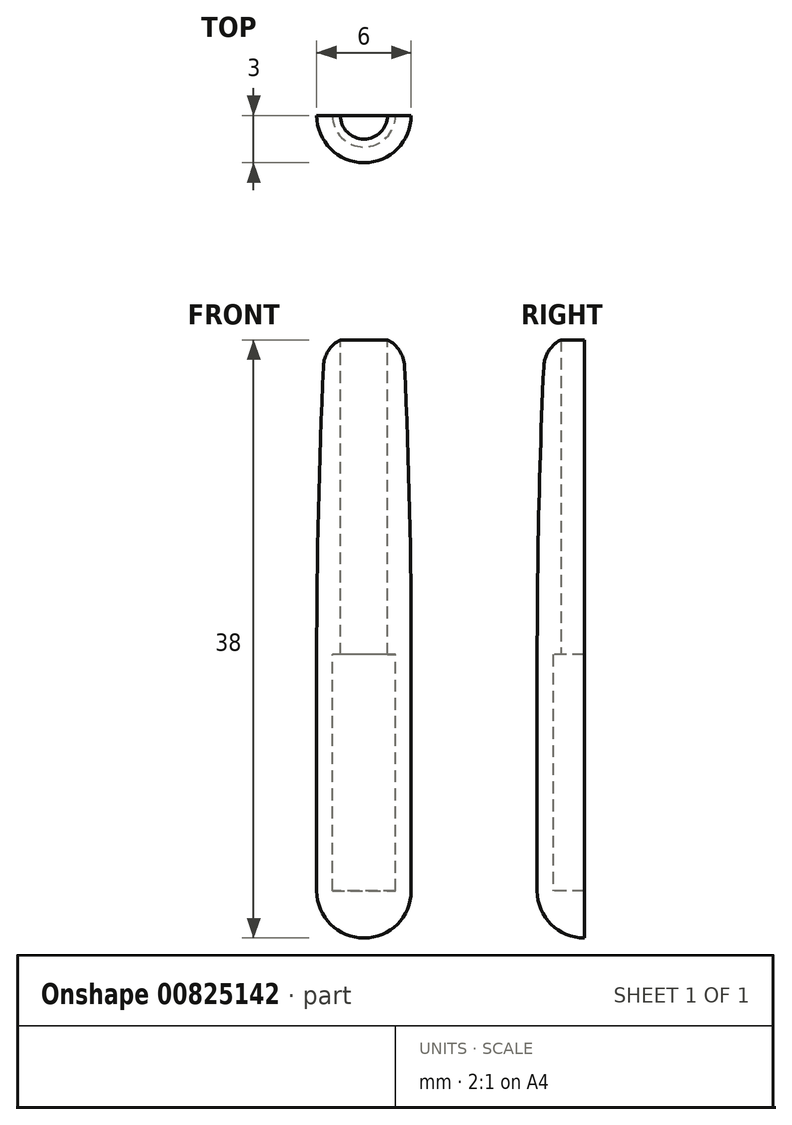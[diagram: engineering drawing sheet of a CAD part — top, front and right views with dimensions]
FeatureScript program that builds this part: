
annotation { "Feature Type Name" : "Feature", "Feature Type Description" : "" }
export const myFeature = defineFeature(function(context is Context, id is Id, definition is map)
    precondition{}
    {
        {
            var Q0;
            Q0=qCreatedBy(makeId("Front.planeOp"),FACE);
            var sketch = newSketch(context, id + "F0", { "sketchPlane" : qUnion([Q0])});
            skCircle(sketch, "E0", {"center": v(0, 0) * mm, "radius": 3 * mm});
            skLineSegment(sketch, "E1", {"start": v(0, 0) * mm, "end": v(0, 15) * mm, "construction": true});
            skLineSegment(sketch, "E2.bottom", {"start": v(2, 0) * mm, "end": v(-2, 0) * mm});
            skLineSegment(sketch, "E2.top", {"start": v(2, 15) * mm, "end": v(-2, 15) * mm});
            skLineSegment(sketch, "E2.left", {"start": v(2, 0) * mm, "end": v(2, 15) * mm});
            skLineSegment(sketch, "E2.right", {"start": v(-2, 0) * mm, "end": v(-2, 15) * mm});
            skPoint(sketch, "E2.middle", {"position": v(0, 7.5) * mm});
            skLineSegment(sketch, "E3", {"start": v(-3, 0) * mm, "end": v(-3, 15) * mm});
            skLineSegment(sketch, "E4.bottom", {"start": v(1.5, 15) * mm, "end": v(-1.5, 15) * mm});
            skLineSegment(sketch, "E4.top", {"start": v(1.5, 35) * mm, "end": v(-1.5, 35) * mm});
            skLineSegment(sketch, "E4.left", {"start": v(1.5, 15) * mm, "end": v(1.5, 35) * mm});
            skLineSegment(sketch, "E4.right", {"start": v(-1.5, 15) * mm, "end": v(-1.5, 35) * mm});
            skPoint(sketch, "E4.middle", {"position": v(0, 25) * mm});
            skArc(sketch, "E5", {"start": v(-2.5, 35) * mm, "mid": v(-2.87, 25) * mm, "end": v(-3, 15) * mm});
            skLineSegment(sketch, "E6", {"start": v(0, 15) * mm, "end": v(0, 38.1) * mm, "construction": true});
            skLineSegment(sketch, "E7", {"start": v(-2.5, 35) * mm, "end": v(-1.5, 35) * mm});
            skLineSegment(sketch, "E8", {"start": v(0, 0) * mm, "end": v(0, -3) * mm});
            skSolve(sketch);
        }
        {
            var Q0;
            {var subQ5=sQuery(id+"F0.wireOp",EDGE,"E8");Q0=makeQuery(id+"F0.imprint","IMPRINT",FACE,{"disambiguationData":[TD([[makeQuery(id+"F0.imprint","IMPRINT",EDGE,{"derivedFrom":subQ5}),-1.0]])]});}
            var Q1;
            {var subQ0=sQuery(id+"F0.wireOp",EDGE,"E3");Q1=makeQuery(id+"F0.imprint","IMPRINT",FACE,{"disambiguationData":[TD([[makeQuery(id+"F0.imprint","IMPRINT",EDGE,{"derivedFrom":subQ0}),-1.0]])]});}
            var Q2;
            Q2=sQuery(id+"F0.wireOp",EDGE,"E1");
            revolve(context, id + "F1", {"surfaceOperationType" : NewSurfaceOperationType.NEW, "entities" : qUnion([Q0, Q1]), "axis" : qUnion([Q2]), "revolveType" : RevolveType.ONE_DIRECTION, "angle" : 180 * degree});
        }
        {
            var Q0;
            Q0=makeQuery(id+"F1.opRevolve","SWEPT_EDGE",EDGE,{"disambiguationData":[OSD([sQuery(id+"F0.wireOp",EDGE,"E5"),sQuery(id+"F0.wireOp",EDGE,"E7")])]});
            fillet(context, id + "F2", {"entities" : qUnion([Q0]), "radius" : 2 * mm, "tangentPropagation" : true, "allowEdgeOverflow" : false});
        }
    });
